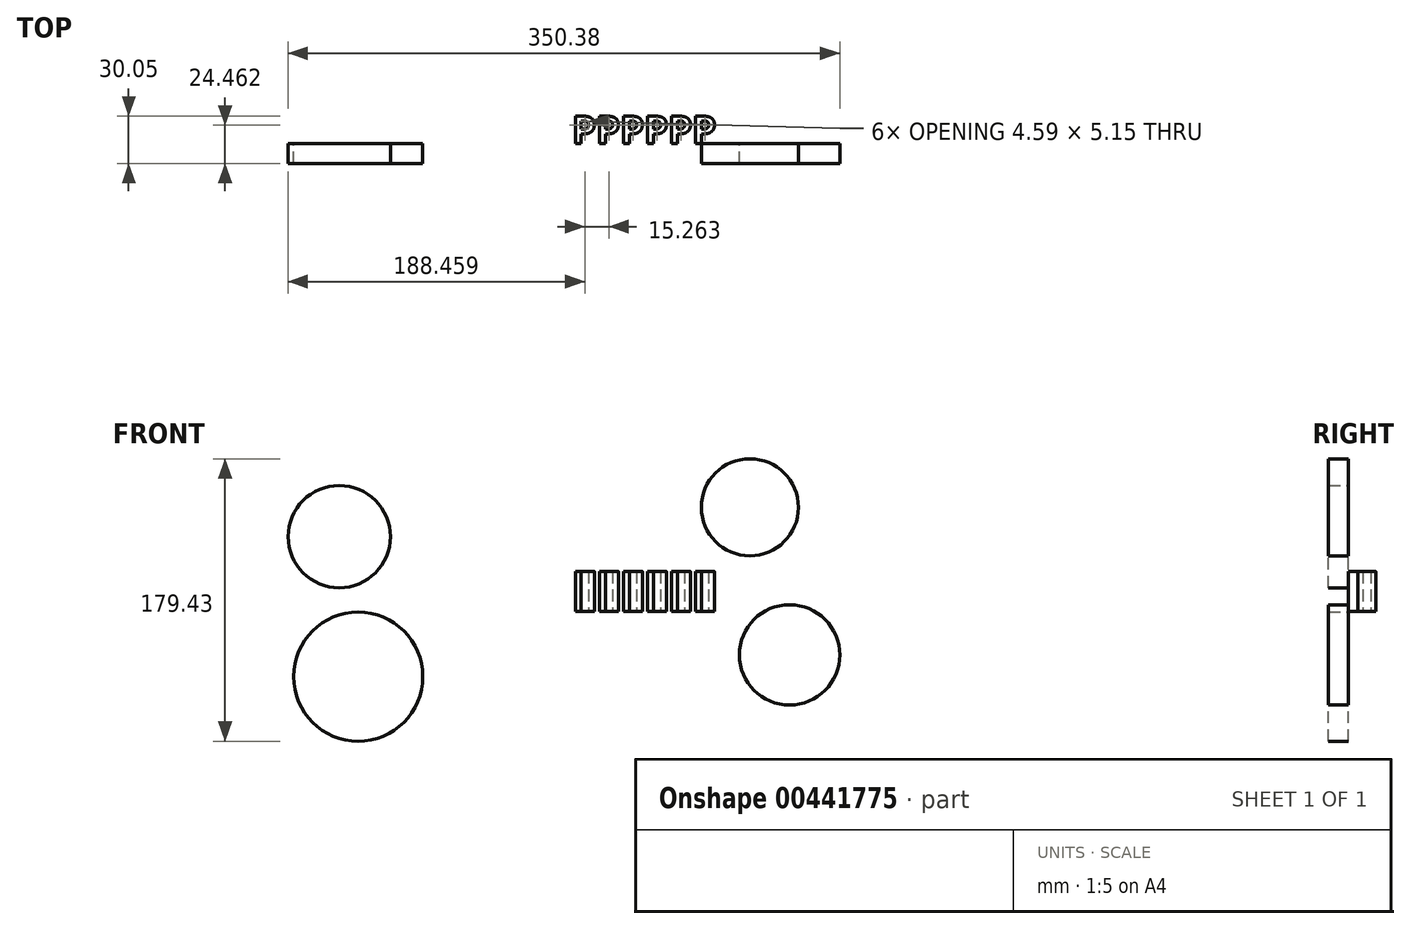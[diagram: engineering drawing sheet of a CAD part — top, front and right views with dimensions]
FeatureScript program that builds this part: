
annotation { "Feature Type Name" : "Feature", "Feature Type Description" : "" }
export const myFeature = defineFeature(function(context is Context, id is Id, definition is map)
    precondition{}
    {
        {
            var Q0;
            Q0=qCreatedBy(makeId("Top.planeOp"),FACE);
            var sketch = newSketch(context, id + "F0", { "sketchPlane" : qUnion([Q0])});
            skText(sketch, "E0", { "text": "PPPPPP\n", "fontName": "OpenSans-Bold.ttf"});
            const initialGuessF0  = {"E0": [0, 0, 1, 0, 0.0175]};
            skSetInitialGuess(sketch, initialGuessF0);
            skSolve(sketch);
        }
        {
            var Q0;
            Q0 = qSketchRegion(id + "F0", true);
            extrude(context, id + "F1", {"entities" : qUnion([Q0]), "depth" : 25.4 * mm});
        }
        {
            var Q0;
            Q0=qCreatedBy(makeId("Front.planeOp"),FACE);
            var sketch = newSketch(context, id + "F2", { "sketchPlane" : qUnion([Q0])});
            skCircle(sketch, "E1", {"center": v(-147.83, 47.47) * mm, "radius": 32.47 * mm});
            skCircle(sketch, "E2", {"center": v(-135.8, -41.46) * mm, "radius": 41.02 * mm});
            skCircle(sketch, "E3", {"center": v(112.97, 66.1) * mm, "radius": 30.84 * mm});
            skCircle(sketch, "E4", {"center": v(138.21, -27.64) * mm, "radius": 31.86 * mm});
            skSolve(sketch);
        }
        {
            var Q0;
            Q0 = qSketchRegion(id + "F2", true);
            extrude(context, id + "F3", {"entities" : qUnion([Q0]), "depth" : 12.7 * mm});
        }
    });
